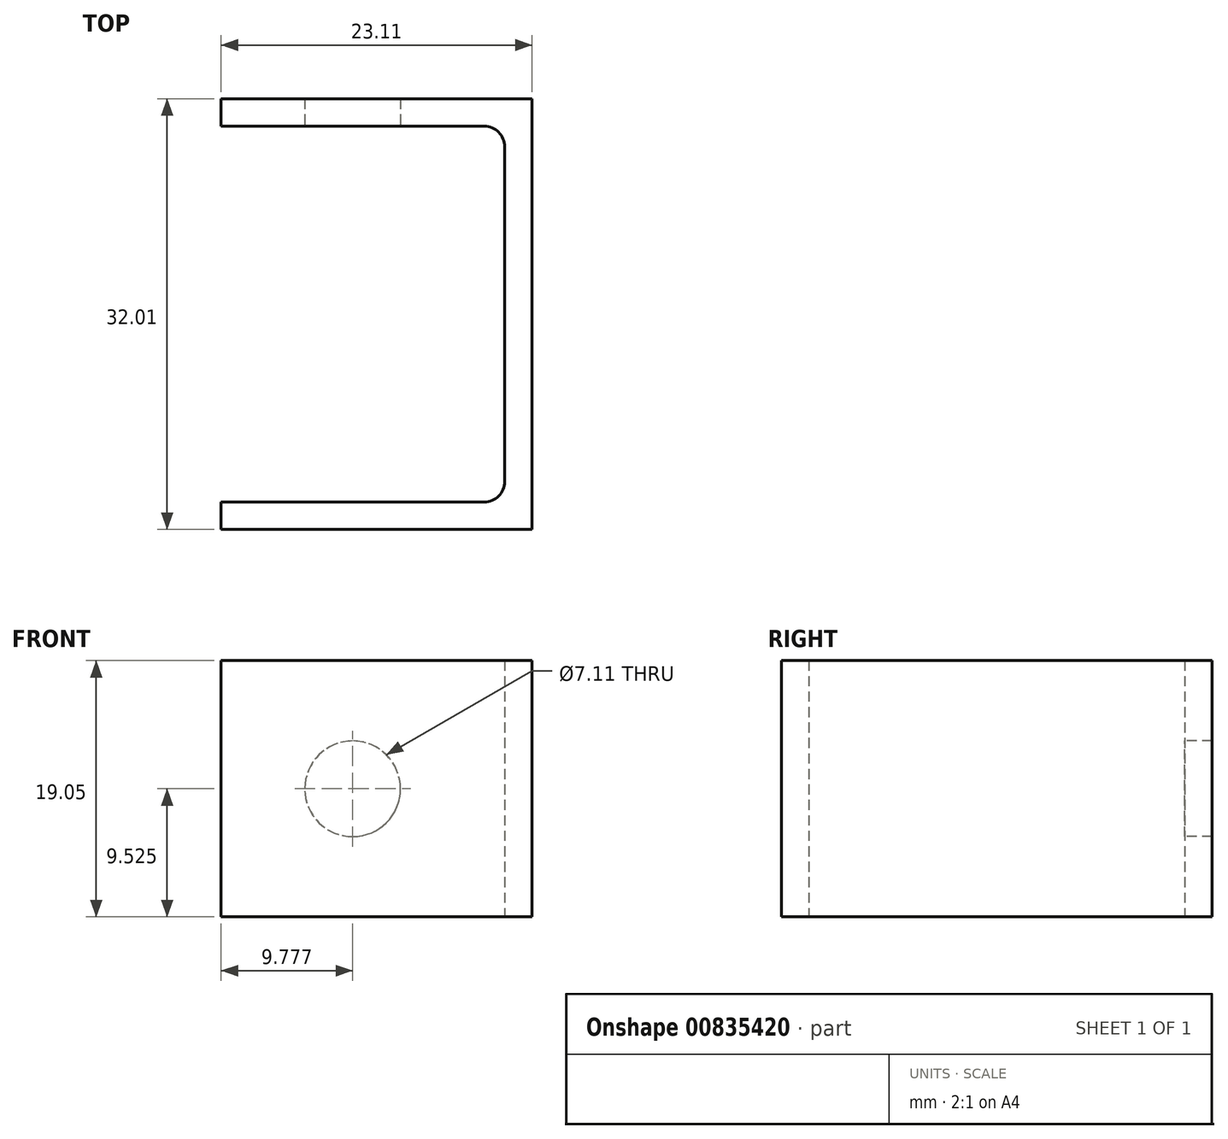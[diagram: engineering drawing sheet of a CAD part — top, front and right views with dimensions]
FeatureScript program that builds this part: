
annotation { "Feature Type Name" : "Feature", "Feature Type Description" : "" }
export const myFeature = defineFeature(function(context is Context, id is Id, definition is map)
    precondition{}
    {
        {
            var Q0;
            Q0=qCreatedBy(makeId("Top.planeOp"),FACE);
            var sketch = newSketch(context, id + "F0", { "sketchPlane" : qUnion([Q0])});
            skLineSegment(sketch, "E0", {"start": v(-19.8, 14.12) * mm, "end": v(-0.23, 14.12) * mm});
            skLineSegment(sketch, "E1", {"start": v(1.3, 12.6) * mm, "end": v(1.3, -12.3) * mm});
            skLineSegment(sketch, "E2", {"start": v(-0.23, -13.82) * mm, "end": v(-19.8, -13.82) * mm});
            skLineSegment(sketch, "E3.0", {"start": v(3.32, -15.85) * mm, "end": v(-19.8, -15.85) * mm});
            skLineSegment(sketch, "E3.1", {"start": v(3.32, 16.16) * mm, "end": v(3.32, -15.85) * mm});
            skLineSegment(sketch, "E3.2", {"start": v(-19.8, 16.16) * mm, "end": v(3.32, 16.16) * mm});
            skLineSegment(sketch, "E4", {"start": v(-19.8, 14.12) * mm, "end": v(-19.8, 16.16) * mm});
            skLineSegment(sketch, "E5", {"start": v(-19.8, -15.85) * mm, "end": v(-19.8, -13.82) * mm});
            skPoint(sketch, "E6.visualSharp", {"position": v(1.3, 14.12) * mm});
            skArc(sketch, "E6.filletArc", {"start": v(1.3, 12.6) * mm, "mid": v(0.84, 13.68) * mm, "end": v(-0.23, 14.12) * mm});
            skPoint(sketch, "E7.visualSharp", {"position": v(1.3, -13.82) * mm});
            skArc(sketch, "E7.filletArc", {"start": v(-0.23, -13.82) * mm, "mid": v(0.84, -13.37) * mm, "end": v(1.3, -12.3) * mm});
            skSolve(sketch);
        }
        {
            var Q0;
            Q0 = qSketchRegion(id + "F0", true);
            extrude(context, id + "F1", {"entities" : qUnion([Q0]), "depth" : 19.05 * mm, "offsetDistance" : 25.4 * mm});
        }
        {
            var Q0;
            Q0=makeQuery(id+"F1.opExtrude","SWEPT_FACE",FACE,{"disambiguationData":[OSD([sQuery(id+"F0.wireOp",EDGE,"E0")])]});
            var sketch = newSketch(context, id + "F2", { "sketchPlane" : qUnion([Q0])});
            skPoint(sketch, "E8", {"position": v(-10.01, 9.53) * mm});
            skPoint(sketch, "E8.positionSnap0", {"position": v(-19.8, 9.53) * mm});
            skPoint(sketch, "E8.positionSnap1", {"position": v(-10.01, 0) * mm});
            skCircle(sketch, "E9", {"center": v(-10.01, 9.53) * mm, "radius": 3.56 * mm});
            skSolve(sketch);
        }
        {
            var Q0;
            Q0 = qSketchRegion(id + "F2", true);
            var Q1;
            Q1=makeQuery(id+"F1.opExtrude","SWEPT_FACE",FACE,{"disambiguationData":[OSD([sQuery(id+"F0.wireOp",EDGE,"E3.2")])]});
            extrude(context, id + "F3", {"entities" : qUnion([Q0]), "operationType" : NewBodyOperationType.REMOVE, "endBound" : BoundingType.UP_TO_SURFACE, "oppositeDirection" : true, "depth" : 25.4 * mm, "endBoundEntityFace" : qUnion([Q1]), "offsetDistance" : 25.4 * mm});
        }
    });
